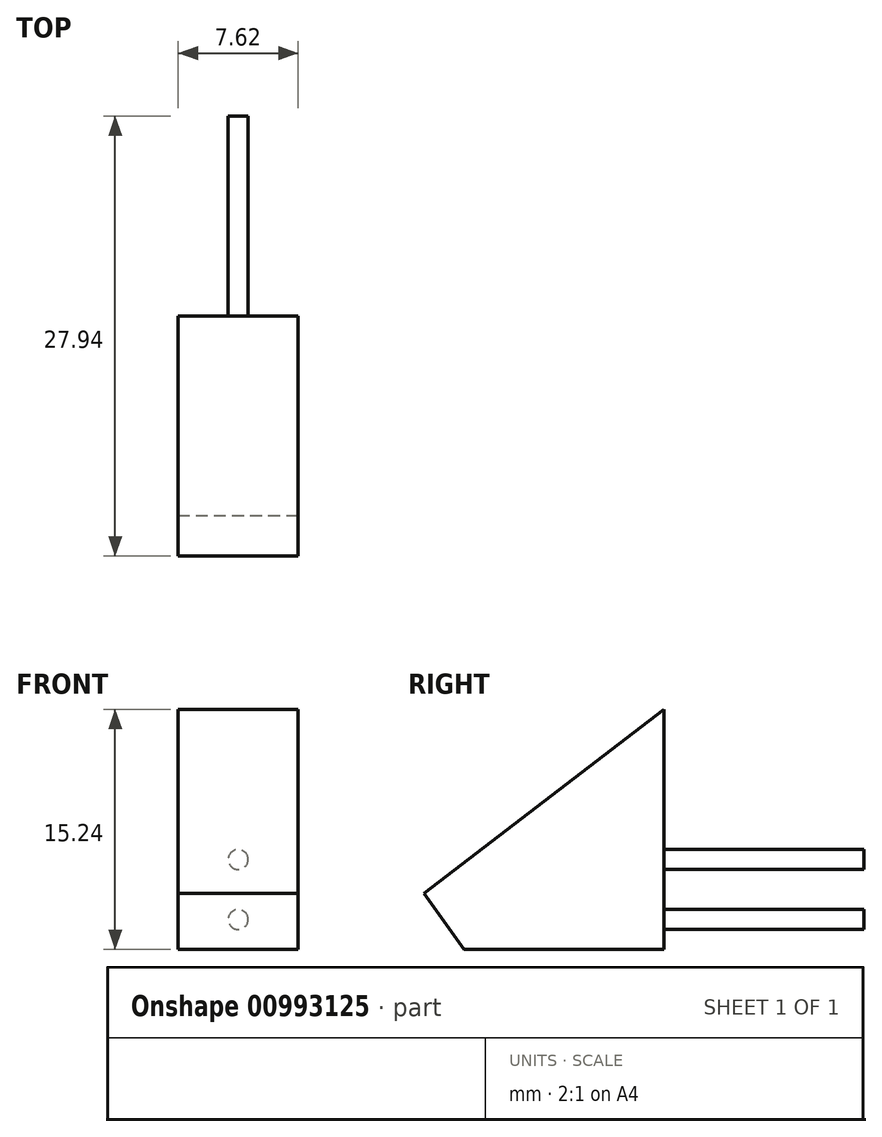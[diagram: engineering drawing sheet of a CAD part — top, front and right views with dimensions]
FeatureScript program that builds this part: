
annotation { "Feature Type Name" : "Feature", "Feature Type Description" : "" }
export const myFeature = defineFeature(function(context is Context, id is Id, definition is map)
    precondition{}
    {
        {
            var Q0;
            Q0=qCreatedBy(makeId("Right.planeOp"),FACE);
            var sketch = newSketch(context, id + "F0", { "sketchPlane" : qUnion([Q0])});
            skLineSegment(sketch, "E0.top", {"start": v(-48.58, 12.92) * mm, "end": v(-35.88, 12.92) * mm});
            skLineSegment(sketch, "E0.right", {"start": v(-35.88, 28.16) * mm, "end": v(-35.88, 12.92) * mm});
            skLineSegment(sketch, "E1", {"start": v(-35.88, 28.16) * mm, "end": v(-51.12, 16.48) * mm});
            skLineSegment(sketch, "E2", {"start": v(-51.12, 16.48) * mm, "end": v(-48.58, 12.92) * mm});
            skSolve(sketch);
        }
        {
            var Q0;
            Q0=makeQuery(id+"F0.imprint","IMPRINT",FACE,{"disambiguationData":[TD([[makeQuery(id+"F0.imprint","IMPRINT",EDGE,{"derivedFrom":sQuery(id+"F0.wireOp",EDGE,"E0.top")}),1.0]])]});
            extrude(context, id + "F1", {"entities" : qUnion([Q0]), "depth" : 7.62 * mm, "offsetDistance" : 25.4 * mm});
        }
        {
            var Q0;
            Q0=makeQuery(id+"F1.opExtrude","SWEPT_FACE",FACE,{"disambiguationData":[OSD([sQuery(id+"F0.wireOp",EDGE,"E0.right")])]});
            var sketch = newSketch(context, id + "F2", { "sketchPlane" : qUnion([Q0])});
            skCircle(sketch, "E3", {"center": v(-3.81, 14.82) * mm, "radius": 0.64 * mm});
            skPoint(sketch, "E3.centerSnap0", {"position": v(-3.81, 12.92) * mm});
            skCircle(sketch, "E4", {"center": v(-3.81, 18.63) * mm, "radius": 0.64 * mm});
            skSolve(sketch);
        }
        {
            var Q0;
            Q0=makeQuery(id+"F2.imprint","IMPRINT",FACE,{"disambiguationData":[TD([[makeQuery(id+"F2.imprint","IMPRINT",EDGE,{"derivedFrom":sQuery(id+"F2.wireOp",EDGE,"E4")}),1.0]])]});
            var Q1;
            Q1=makeQuery(id+"F2.imprint","IMPRINT",FACE,{"disambiguationData":[TD([[makeQuery(id+"F2.imprint","IMPRINT",EDGE,{"derivedFrom":sQuery(id+"F2.wireOp",EDGE,"E3")}),1.0]])]});
            extrude(context, id + "F3", {"entities" : qUnion([Q0, Q1]), "operationType" : NewBodyOperationType.ADD, "depth" : 12.7 * mm, "offsetDistance" : 25.4 * mm});
        }
    });
